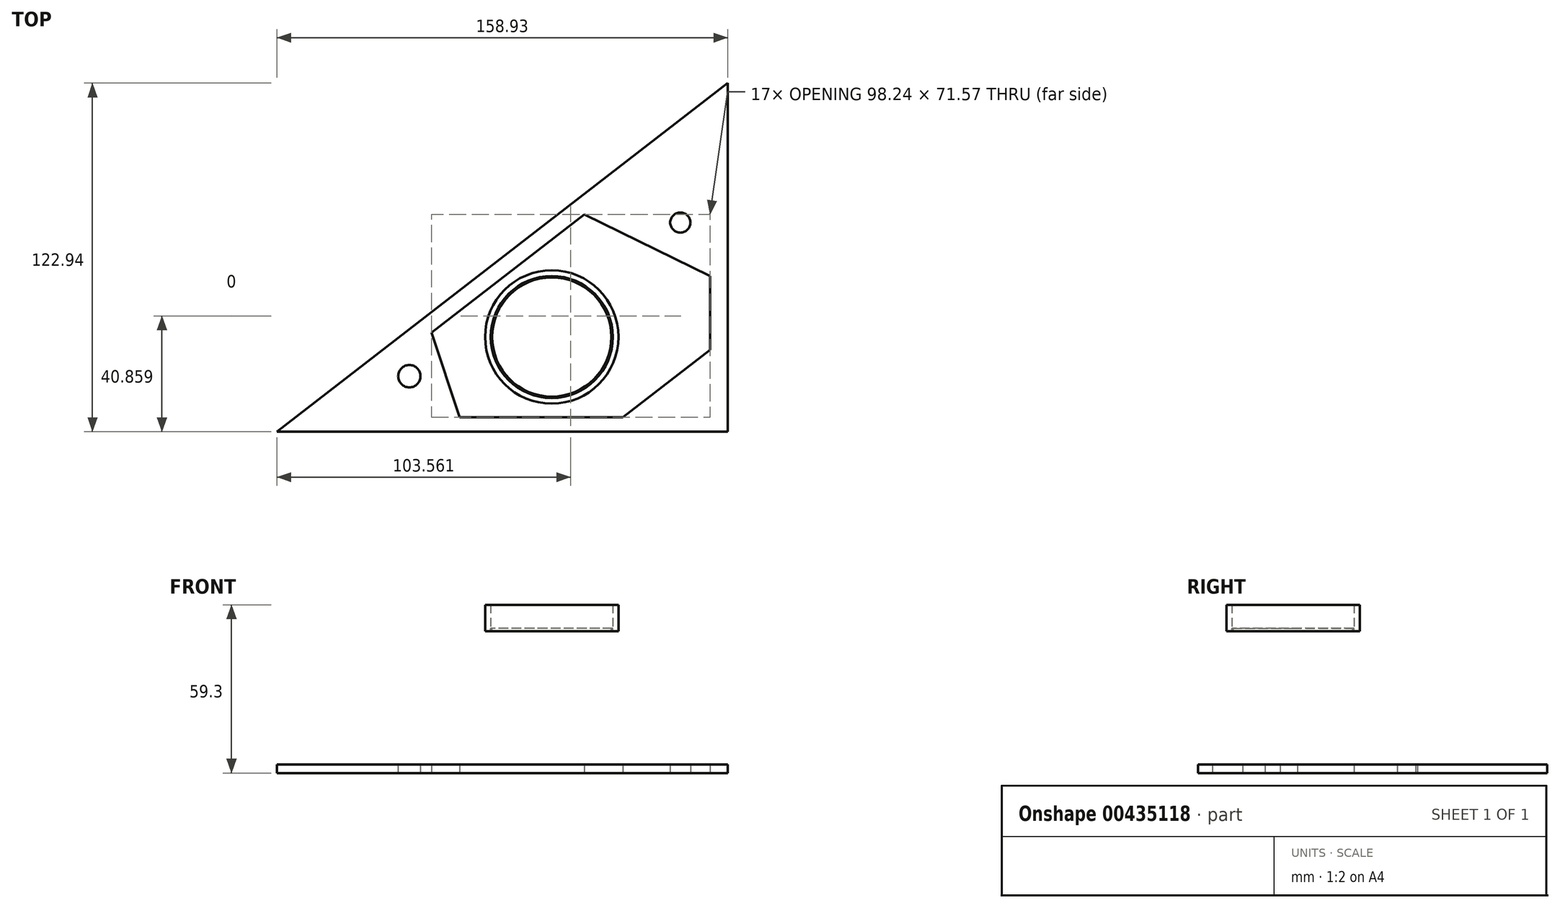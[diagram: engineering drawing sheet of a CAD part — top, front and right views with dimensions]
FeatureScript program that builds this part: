
annotation { "Feature Type Name" : "Feature", "Feature Type Description" : "" }
export const myFeature = defineFeature(function(context is Context, id is Id, definition is map)
    precondition{}
    {
        {
            var Q0;
            Q0=qCreatedBy(makeId("Top.planeOp"),FACE);
            var sketch = newSketch(context, id + "F0", { "sketchPlane" : qUnion([Q0])});
            skCircle(sketch, "E0", {"center": v(0, 0) * mm, "radius": 21.5 * mm});
            skLineSegment(sketch, "E1", {"start": v(-96.87, -33.42) * mm, "end": v(62.06, -33.42) * mm});
            skLineSegment(sketch, "E2", {"start": v(62.06, -33.42) * mm, "end": v(62.06, 89.52) * mm});
            skLineSegment(sketch, "E3", {"start": v(62.06, 89.52) * mm, "end": v(-96.87, -33.42) * mm});
            skCircle(sketch, "E4", {"center": v(-50.2, -13.82) * mm, "radius": 3.94 * mm});
            skCircle(sketch, "E5", {"center": v(45.3, 40.34) * mm, "radius": 3.56 * mm});
            skCircle(sketch, "E6", {"center": v(0, 0) * mm, "radius": 21 * mm});
            skCircle(sketch, "E7", {"center": v(0, 0) * mm, "radius": 23.5 * mm});
            skLineSegment(sketch, "E8", {"start": v(55.81, 21.48) * mm, "end": v(11.45, 43.23) * mm});
            skLineSegment(sketch, "E9", {"start": v(5.8, 46) * mm, "end": v(-44.32, 7.23) * mm});
            skLineSegment(sketch, "E10", {"start": v(-42.43, 1.55) * mm, "end": v(-32.5, -28.35) * mm});
            skLineSegment(sketch, "E11", {"start": v(-30.8, -33.42) * mm, "end": v(18.49, -33.42) * mm});
            skLineSegment(sketch, "E12", {"start": v(25.05, -28.35) * mm, "end": v(55.81, -4.55) * mm});
            skLineSegment(sketch, "E13", {"start": v(11.45, 43.23) * mm, "end": v(-42.43, 1.55) * mm});
            skLineSegment(sketch, "E14", {"start": v(-32.5, -28.35) * mm, "end": v(25.05, -28.35) * mm});
            skLineSegment(sketch, "E15", {"start": v(55.81, -4.55) * mm, "end": v(55.81, 21.48) * mm});
            skPoint(sketch, "E16.orphan", {"position": v(61.7, 0) * mm});
            skSolve(sketch);
        }
        {
            var Q0;
            Q0=makeQuery(id+"F0.imprint","IMPRINT",FACE,{"disambiguationData":[TD([[makeQuery(id+"F0.imprint","IMPRINT",EDGE,{"derivedFrom":sQuery(id+"F0.wireOp",EDGE,"E0")}),1.0]])]});
            extrude(context, id + "F1", {"entities" : qUnion([Q0]), "oppositeDirection" : true, "depth" : 1 * mm});
        }
        {
            var Q0;
            Q0=makeQuery(id+"F0.imprint","IMPRINT",FACE,{"disambiguationData":[TD([[makeQuery(id+"F0.imprint","IMPRINT",EDGE,{"derivedFrom":sQuery(id+"F0.wireOp",EDGE,"E0")}),-1.0]])]});
            extrude(context, id + "F2", {"entities" : qUnion([Q0]), "depth" : 9.3 * mm});
        }
        {
            var Q0;
            Q0=makeQuery(id+"F2.opExtrude","SWEPT_BODY",BODY,{"disambiguationData":[OSD([sQuery(id+"F0.wireOp",EDGE,"E0"),sQuery(id+"F0.wireOp",EDGE,"E7")])]});
            var Q1;
            Q1=makeQuery(id+"F1.opExtrude","SWEPT_BODY",BODY,{"disambiguationData":[OSD([sQuery(id+"F0.wireOp",EDGE,"E6")])]});
            var Q2;
            Q2=sQuery(id+"F0.wireOp",EDGE,"E7");
            var Q3;
            Q3=makeQuery(id+"F1.opExtrude","CAP_EDGE",EDGE,{"disambiguationData":[OSD([sQuery(id+"F0.wireOp",EDGE,"E7")])],"isStart":false});
            var Q4;
            Q4=qCreatedBy(makeId("Top.planeOp"),FACE);
            transform(context, id + "F3", {"entities" : qUnion([Q0, Q1]), "transformType" : TransformType.TRANSLATION_DISTANCE, "transformDirection" : qUnion([Q4]), "distance" : 50 * mm, "makeCopy" : false});
        }
        {
            var Q0;
            {var subQ5=sQuery(id+"F0.wireOp",EDGE,"E2");Q0=makeQuery(id+"F0.imprint","IMPRINT",FACE,{"disambiguationData":[TD([[makeQuery(id+"F0.imprint","IMPRINT",EDGE,{"derivedFrom":subQ5}),1.0]])]});}
            extrude(context, id + "F4", {"entities" : qUnion([Q0]), "depth" : 3 * mm});
        }
        {
            var Q0;
            Q0=makeQuery(id+"F1.opExtrude","SWEPT_BODY",BODY,{"disambiguationData":[OSD([sQuery(id+"F0.wireOp",EDGE,"E0"),sQuery(id+"F0.wireOp",EDGE,"E6")])]});
            transform(context, id + "F5", {"entities" : qUnion([Q0]), "transformType" : TransformType.TRANSLATION_3D, "dx" : 0 * mm, "dy" : 0 * mm, "dz" : 1 * mm, "makeCopy" : false});
        }
    });
